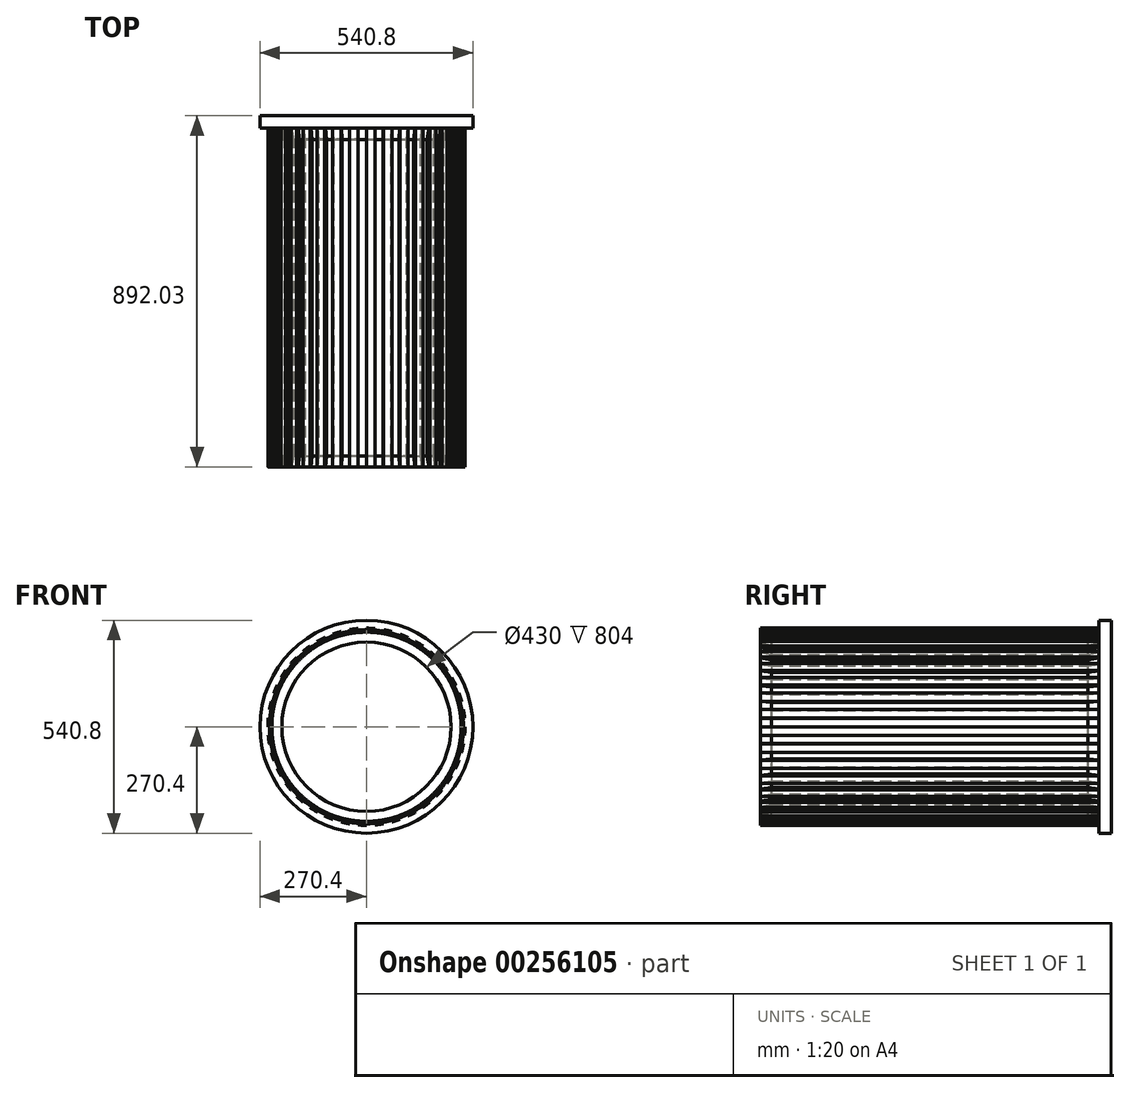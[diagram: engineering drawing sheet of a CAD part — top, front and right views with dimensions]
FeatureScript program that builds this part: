
annotation { "Feature Type Name" : "Feature", "Feature Type Description" : "" }
export const myFeature = defineFeature(function(context is Context, id is Id, definition is map)
    precondition{}
    {
        {
            var Q0;
            Q0=qCreatedBy(makeId("Front.planeOp"),FACE);
            var sketch = newSketch(context, id + "F0", { "sketchPlane" : qUnion([Q0])});
            skArc(sketch, "E0", {"start": v(-249.45, 21.82) * mm, "mid": v(-250.16, 10.92) * mm, "end": v(-250.4, 0) * mm});
            skArc(sketch, "E1", {"start": v(-236.75, 41.75) * mm, "mid": v(-238.34, 31.38) * mm, "end": v(-239.49, 20.95) * mm});
            skLineSegment(sketch, "E2", {"start": v(-239.49, 20.95) * mm, "end": v(-249.45, 21.82) * mm});
            skLineSegment(sketch, "E3", {"start": v(-236.75, 41.75) * mm, "end": v(-246.6, 43.48) * mm});
            skLineSegment(sketch, "E4.anchor1", {"start": v(0, 0) * mm, "end": v(-250.4, 0) * mm, "construction": true});
            skLineSegment(sketch, "E4.anchor2", {"start": v(0, 0) * mm, "end": v(-250.4, 0) * mm, "construction": true});
            skLineSegment(sketch, "E5.1.0", {"start": v(-225.9, 82.22) * mm, "end": v(-235.3, 85.64) * mm});
            skArc(sketch, "E5.1.1", {"start": v(-241.87, 64.8) * mm, "mid": v(-244.46, 54.2) * mm, "end": v(-246.6, 43.48) * mm});
            skLineSegment(sketch, "E5.1.2", {"start": v(-232.2, 62.22) * mm, "end": v(-241.87, 64.8) * mm});
            skArc(sketch, "E5.1.3", {"start": v(-225.9, 82.22) * mm, "mid": v(-229.27, 72.29) * mm, "end": v(-232.2, 62.22) * mm});
            skLineSegment(sketch, "E5.1.4", {"start": v(-225.9, 82.22) * mm, "end": v(-235.3, 85.64) * mm});
            skArc(sketch, "E5.1.5", {"start": v(-241.87, 64.8) * mm, "mid": v(-244.46, 54.2) * mm, "end": v(-246.6, 43.48) * mm});
            skLineSegment(sketch, "E5.1.6", {"start": v(-232.2, 62.22) * mm, "end": v(-241.87, 64.8) * mm});
            skArc(sketch, "E5.1.7", {"start": v(-225.9, 82.22) * mm, "mid": v(-229.27, 72.29) * mm, "end": v(-232.2, 62.22) * mm});
            skLineSegment(sketch, "E5.1.8", {"start": v(-225.9, 82.22) * mm, "end": v(-235.3, 85.64) * mm});
            skLineSegment(sketch, "E5.1.9", {"start": v(-232.2, 62.22) * mm, "end": v(-241.87, 64.8) * mm});
            skArc(sketch, "E5.1.10", {"start": v(-225.9, 82.22) * mm, "mid": v(-229.27, 72.29) * mm, "end": v(-232.2, 62.22) * mm});
            skArc(sketch, "E5.1.11", {"start": v(-241.87, 64.8) * mm, "mid": v(-244.46, 54.2) * mm, "end": v(-246.6, 43.48) * mm});
            skLineSegment(sketch, "E5.2.0", {"start": v(-208.2, 120.2) * mm, "end": v(-216.85, 125.2) * mm});
            skArc(sketch, "E5.2.1", {"start": v(-226.94, 105.82) * mm, "mid": v(-231.34, 95.82) * mm, "end": v(-235.3, 85.64) * mm});
            skLineSegment(sketch, "E5.2.2", {"start": v(-217.88, 101.6) * mm, "end": v(-226.94, 105.82) * mm});
            skArc(sketch, "E5.2.3", {"start": v(-208.2, 120.2) * mm, "mid": v(-213.24, 111) * mm, "end": v(-217.88, 101.6) * mm});
            skLineSegment(sketch, "E5.2.4", {"start": v(-208.2, 120.2) * mm, "end": v(-216.85, 125.2) * mm});
            skArc(sketch, "E5.2.5", {"start": v(-226.94, 105.82) * mm, "mid": v(-231.34, 95.82) * mm, "end": v(-235.3, 85.64) * mm});
            skLineSegment(sketch, "E5.2.6", {"start": v(-217.88, 101.6) * mm, "end": v(-226.94, 105.82) * mm});
            skArc(sketch, "E5.2.7", {"start": v(-208.2, 120.2) * mm, "mid": v(-213.24, 111) * mm, "end": v(-217.88, 101.6) * mm});
            skLineSegment(sketch, "E5.2.8", {"start": v(-208.2, 120.2) * mm, "end": v(-216.85, 125.2) * mm});
            skLineSegment(sketch, "E5.2.9", {"start": v(-217.88, 101.6) * mm, "end": v(-226.94, 105.82) * mm});
            skArc(sketch, "E5.2.10", {"start": v(-208.2, 120.2) * mm, "mid": v(-213.24, 111) * mm, "end": v(-217.88, 101.6) * mm});
            skArc(sketch, "E5.2.11", {"start": v(-226.94, 105.82) * mm, "mid": v(-231.34, 95.82) * mm, "end": v(-235.3, 85.64) * mm});
            skLineSegment(sketch, "E5.3.0", {"start": v(-184.16, 154.53) * mm, "end": v(-191.82, 160.95) * mm});
            skArc(sketch, "E5.3.1", {"start": v(-205.12, 143.62) * mm, "mid": v(-211.19, 134.54) * mm, "end": v(-216.85, 125.2) * mm});
            skLineSegment(sketch, "E5.3.2", {"start": v(-196.92, 137.89) * mm, "end": v(-205.12, 143.62) * mm});
            skArc(sketch, "E5.3.3", {"start": v(-184.16, 154.53) * mm, "mid": v(-190.72, 146.35) * mm, "end": v(-196.92, 137.89) * mm});
            skLineSegment(sketch, "E5.3.4", {"start": v(-184.16, 154.53) * mm, "end": v(-191.82, 160.95) * mm});
            skArc(sketch, "E5.3.5", {"start": v(-205.12, 143.62) * mm, "mid": v(-211.19, 134.54) * mm, "end": v(-216.85, 125.2) * mm});
            skLineSegment(sketch, "E5.3.6", {"start": v(-196.92, 137.89) * mm, "end": v(-205.12, 143.62) * mm});
            skArc(sketch, "E5.3.7", {"start": v(-184.16, 154.53) * mm, "mid": v(-190.72, 146.35) * mm, "end": v(-196.92, 137.89) * mm});
            skLineSegment(sketch, "E5.3.8", {"start": v(-184.16, 154.53) * mm, "end": v(-191.82, 160.95) * mm});
            skLineSegment(sketch, "E5.3.9", {"start": v(-196.92, 137.89) * mm, "end": v(-205.12, 143.62) * mm});
            skArc(sketch, "E5.3.10", {"start": v(-184.16, 154.53) * mm, "mid": v(-190.72, 146.35) * mm, "end": v(-196.92, 137.89) * mm});
            skArc(sketch, "E5.3.11", {"start": v(-205.12, 143.62) * mm, "mid": v(-211.19, 134.54) * mm, "end": v(-216.85, 125.2) * mm});
            skLineSegment(sketch, "E5.4.0", {"start": v(-154.53, 184.16) * mm, "end": v(-160.95, 191.82) * mm});
            skArc(sketch, "E5.4.1", {"start": v(-177.06, 177.06) * mm, "mid": v(-184.61, 169.17) * mm, "end": v(-191.82, 160.95) * mm});
            skLineSegment(sketch, "E5.4.2", {"start": v(-169.99, 169.99) * mm, "end": v(-177.06, 177.06) * mm});
            skArc(sketch, "E5.4.3", {"start": v(-154.53, 184.16) * mm, "mid": v(-162.41, 177.24) * mm, "end": v(-169.99, 169.99) * mm});
            skLineSegment(sketch, "E5.4.4", {"start": v(-154.53, 184.16) * mm, "end": v(-160.95, 191.82) * mm});
            skArc(sketch, "E5.4.5", {"start": v(-177.06, 177.06) * mm, "mid": v(-184.61, 169.17) * mm, "end": v(-191.82, 160.95) * mm});
            skLineSegment(sketch, "E5.4.6", {"start": v(-169.99, 169.99) * mm, "end": v(-177.06, 177.06) * mm});
            skArc(sketch, "E5.4.7", {"start": v(-154.53, 184.16) * mm, "mid": v(-162.41, 177.24) * mm, "end": v(-169.99, 169.99) * mm});
            skLineSegment(sketch, "E5.4.8", {"start": v(-154.53, 184.16) * mm, "end": v(-160.95, 191.82) * mm});
            skLineSegment(sketch, "E5.4.9", {"start": v(-169.99, 169.99) * mm, "end": v(-177.06, 177.06) * mm});
            skArc(sketch, "E5.4.10", {"start": v(-154.53, 184.16) * mm, "mid": v(-162.41, 177.24) * mm, "end": v(-169.99, 169.99) * mm});
            skArc(sketch, "E5.4.11", {"start": v(-177.06, 177.06) * mm, "mid": v(-184.61, 169.17) * mm, "end": v(-191.82, 160.95) * mm});
            skLineSegment(sketch, "E5.5.0", {"start": v(-120.2, 208.2) * mm, "end": v(-125.2, 216.85) * mm});
            skArc(sketch, "E5.5.1", {"start": v(-143.62, 205.12) * mm, "mid": v(-152.43, 198.66) * mm, "end": v(-160.95, 191.82) * mm});
            skLineSegment(sketch, "E5.5.2", {"start": v(-137.89, 196.92) * mm, "end": v(-143.62, 205.12) * mm});
            skArc(sketch, "E5.5.3", {"start": v(-120.2, 208.2) * mm, "mid": v(-129.17, 202.75) * mm, "end": v(-137.89, 196.92) * mm});
            skLineSegment(sketch, "E5.5.4", {"start": v(-120.2, 208.2) * mm, "end": v(-125.2, 216.85) * mm});
            skArc(sketch, "E5.5.5", {"start": v(-143.62, 205.12) * mm, "mid": v(-152.43, 198.66) * mm, "end": v(-160.95, 191.82) * mm});
            skLineSegment(sketch, "E5.5.6", {"start": v(-137.89, 196.92) * mm, "end": v(-143.62, 205.12) * mm});
            skArc(sketch, "E5.5.7", {"start": v(-120.2, 208.2) * mm, "mid": v(-129.17, 202.75) * mm, "end": v(-137.89, 196.92) * mm});
            skLineSegment(sketch, "E5.5.8", {"start": v(-120.2, 208.2) * mm, "end": v(-125.2, 216.85) * mm});
            skLineSegment(sketch, "E5.5.9", {"start": v(-137.89, 196.92) * mm, "end": v(-143.62, 205.12) * mm});
            skArc(sketch, "E5.5.10", {"start": v(-120.2, 208.2) * mm, "mid": v(-129.17, 202.75) * mm, "end": v(-137.89, 196.92) * mm});
            skArc(sketch, "E5.5.11", {"start": v(-143.62, 205.12) * mm, "mid": v(-152.43, 198.66) * mm, "end": v(-160.95, 191.82) * mm});
            skLineSegment(sketch, "E5.6.0", {"start": v(-82.22, 225.9) * mm, "end": v(-85.64, 235.3) * mm});
            skArc(sketch, "E5.6.1", {"start": v(-105.82, 226.94) * mm, "mid": v(-115.62, 222.1) * mm, "end": v(-125.2, 216.85) * mm});
            skLineSegment(sketch, "E5.6.2", {"start": v(-101.6, 217.88) * mm, "end": v(-105.82, 226.94) * mm});
            skArc(sketch, "E5.6.3", {"start": v(-82.22, 225.9) * mm, "mid": v(-92, 222.1) * mm, "end": v(-101.6, 217.88) * mm});
            skLineSegment(sketch, "E5.6.4", {"start": v(-82.22, 225.9) * mm, "end": v(-85.64, 235.3) * mm});
            skArc(sketch, "E5.6.5", {"start": v(-105.82, 226.94) * mm, "mid": v(-115.62, 222.1) * mm, "end": v(-125.2, 216.85) * mm});
            skLineSegment(sketch, "E5.6.6", {"start": v(-101.6, 217.88) * mm, "end": v(-105.82, 226.94) * mm});
            skArc(sketch, "E5.6.7", {"start": v(-82.22, 225.9) * mm, "mid": v(-92, 222.1) * mm, "end": v(-101.6, 217.88) * mm});
            skLineSegment(sketch, "E5.6.8", {"start": v(-82.22, 225.9) * mm, "end": v(-85.64, 235.3) * mm});
            skLineSegment(sketch, "E5.6.9", {"start": v(-101.6, 217.88) * mm, "end": v(-105.82, 226.94) * mm});
            skArc(sketch, "E5.6.10", {"start": v(-82.22, 225.9) * mm, "mid": v(-92, 222.1) * mm, "end": v(-101.6, 217.88) * mm});
            skArc(sketch, "E5.6.11", {"start": v(-105.82, 226.94) * mm, "mid": v(-115.62, 222.1) * mm, "end": v(-125.2, 216.85) * mm});
            skLineSegment(sketch, "E5.7.0", {"start": v(-41.75, 236.75) * mm, "end": v(-43.48, 246.6) * mm});
            skArc(sketch, "E5.7.1", {"start": v(-64.8, 241.87) * mm, "mid": v(-75.3, 238.81) * mm, "end": v(-85.64, 235.3) * mm});
            skLineSegment(sketch, "E5.7.2", {"start": v(-62.22, 232.2) * mm, "end": v(-64.8, 241.87) * mm});
            skArc(sketch, "E5.7.3", {"start": v(-41.75, 236.75) * mm, "mid": v(-52.03, 234.7) * mm, "end": v(-62.22, 232.2) * mm});
            skLineSegment(sketch, "E5.7.4", {"start": v(-41.75, 236.75) * mm, "end": v(-43.48, 246.6) * mm});
            skArc(sketch, "E5.7.5", {"start": v(-64.8, 241.87) * mm, "mid": v(-75.3, 238.81) * mm, "end": v(-85.64, 235.3) * mm});
            skLineSegment(sketch, "E5.7.6", {"start": v(-62.22, 232.2) * mm, "end": v(-64.8, 241.87) * mm});
            skArc(sketch, "E5.7.7", {"start": v(-41.75, 236.75) * mm, "mid": v(-52.03, 234.7) * mm, "end": v(-62.22, 232.2) * mm});
            skLineSegment(sketch, "E5.7.8", {"start": v(-41.75, 236.75) * mm, "end": v(-43.48, 246.6) * mm});
            skLineSegment(sketch, "E5.7.9", {"start": v(-62.22, 232.2) * mm, "end": v(-64.8, 241.87) * mm});
            skArc(sketch, "E5.7.10", {"start": v(-41.75, 236.75) * mm, "mid": v(-52.03, 234.7) * mm, "end": v(-62.22, 232.2) * mm});
            skArc(sketch, "E5.7.11", {"start": v(-64.8, 241.87) * mm, "mid": v(-75.3, 238.81) * mm, "end": v(-85.64, 235.3) * mm});
            skLineSegment(sketch, "E5.8.0", {"start": v(0, 240.4) * mm, "end": v(0, 250.4) * mm});
            skArc(sketch, "E5.8.1", {"start": v(-21.82, 249.45) * mm, "mid": v(-32.68, 248.26) * mm, "end": v(-43.48, 246.6) * mm});
            skLineSegment(sketch, "E5.8.2", {"start": v(-20.95, 239.49) * mm, "end": v(-21.82, 249.45) * mm});
            skArc(sketch, "E5.8.3", {"start": v(0, 240.4) * mm, "mid": v(-10.49, 240.17) * mm, "end": v(-20.95, 239.49) * mm});
            skLineSegment(sketch, "E5.8.4", {"start": v(0, 240.4) * mm, "end": v(0, 250.4) * mm});
            skArc(sketch, "E5.8.5", {"start": v(-21.82, 249.45) * mm, "mid": v(-32.68, 248.26) * mm, "end": v(-43.48, 246.6) * mm});
            skLineSegment(sketch, "E5.8.6", {"start": v(-20.95, 239.49) * mm, "end": v(-21.82, 249.45) * mm});
            skArc(sketch, "E5.8.7", {"start": v(0, 240.4) * mm, "mid": v(-10.49, 240.17) * mm, "end": v(-20.95, 239.49) * mm});
            skLineSegment(sketch, "E5.8.8", {"start": v(0, 240.4) * mm, "end": v(0, 250.4) * mm});
            skLineSegment(sketch, "E5.8.9", {"start": v(-20.95, 239.49) * mm, "end": v(-21.82, 249.45) * mm});
            skArc(sketch, "E5.8.10", {"start": v(0, 240.4) * mm, "mid": v(-10.49, 240.17) * mm, "end": v(-20.95, 239.49) * mm});
            skArc(sketch, "E5.8.11", {"start": v(-21.82, 249.45) * mm, "mid": v(-32.68, 248.26) * mm, "end": v(-43.48, 246.6) * mm});
            skLineSegment(sketch, "E5.9.0", {"start": v(41.75, 236.75) * mm, "end": v(43.48, 246.6) * mm});
            skArc(sketch, "E5.9.1", {"start": v(21.82, 249.45) * mm, "mid": v(10.92, 250.16) * mm, "end": v(0, 250.4) * mm});
            skLineSegment(sketch, "E5.9.2", {"start": v(20.95, 239.49) * mm, "end": v(21.82, 249.45) * mm});
            skArc(sketch, "E5.9.3", {"start": v(41.75, 236.75) * mm, "mid": v(31.38, 238.34) * mm, "end": v(20.95, 239.49) * mm});
            skLineSegment(sketch, "E5.9.4", {"start": v(41.75, 236.75) * mm, "end": v(43.48, 246.6) * mm});
            skArc(sketch, "E5.9.5", {"start": v(21.82, 249.45) * mm, "mid": v(10.92, 250.16) * mm, "end": v(0, 250.4) * mm});
            skLineSegment(sketch, "E5.9.6", {"start": v(20.95, 239.49) * mm, "end": v(21.82, 249.45) * mm});
            skArc(sketch, "E5.9.7", {"start": v(41.75, 236.75) * mm, "mid": v(31.38, 238.34) * mm, "end": v(20.95, 239.49) * mm});
            skLineSegment(sketch, "E5.9.8", {"start": v(41.75, 236.75) * mm, "end": v(43.48, 246.6) * mm});
            skLineSegment(sketch, "E5.9.9", {"start": v(20.95, 239.49) * mm, "end": v(21.82, 249.45) * mm});
            skArc(sketch, "E5.9.10", {"start": v(41.75, 236.75) * mm, "mid": v(31.38, 238.34) * mm, "end": v(20.95, 239.49) * mm});
            skArc(sketch, "E5.9.11", {"start": v(21.82, 249.45) * mm, "mid": v(10.92, 250.16) * mm, "end": v(0, 250.4) * mm});
            skLineSegment(sketch, "E5.10.0", {"start": v(82.22, 225.9) * mm, "end": v(85.64, 235.3) * mm});
            skArc(sketch, "E5.10.1", {"start": v(64.8, 241.87) * mm, "mid": v(54.2, 244.46) * mm, "end": v(43.48, 246.6) * mm});
            skLineSegment(sketch, "E5.10.2", {"start": v(62.22, 232.2) * mm, "end": v(64.8, 241.87) * mm});
            skArc(sketch, "E5.10.3", {"start": v(82.22, 225.9) * mm, "mid": v(72.29, 229.27) * mm, "end": v(62.22, 232.2) * mm});
            skLineSegment(sketch, "E5.10.4", {"start": v(82.22, 225.9) * mm, "end": v(85.64, 235.3) * mm});
            skArc(sketch, "E5.10.5", {"start": v(64.8, 241.87) * mm, "mid": v(54.2, 244.46) * mm, "end": v(43.48, 246.6) * mm});
            skLineSegment(sketch, "E5.10.6", {"start": v(62.22, 232.2) * mm, "end": v(64.8, 241.87) * mm});
            skArc(sketch, "E5.10.7", {"start": v(82.22, 225.9) * mm, "mid": v(72.29, 229.27) * mm, "end": v(62.22, 232.2) * mm});
            skLineSegment(sketch, "E5.10.8", {"start": v(82.22, 225.9) * mm, "end": v(85.64, 235.3) * mm});
            skLineSegment(sketch, "E5.10.9", {"start": v(62.22, 232.2) * mm, "end": v(64.8, 241.87) * mm});
            skArc(sketch, "E5.10.10", {"start": v(82.22, 225.9) * mm, "mid": v(72.29, 229.27) * mm, "end": v(62.22, 232.2) * mm});
            skArc(sketch, "E5.10.11", {"start": v(64.8, 241.87) * mm, "mid": v(54.2, 244.46) * mm, "end": v(43.48, 246.6) * mm});
            skLineSegment(sketch, "E5.11.0", {"start": v(120.2, 208.2) * mm, "end": v(125.2, 216.85) * mm});
            skArc(sketch, "E5.11.1", {"start": v(105.82, 226.94) * mm, "mid": v(95.82, 231.34) * mm, "end": v(85.64, 235.3) * mm});
            skLineSegment(sketch, "E5.11.2", {"start": v(101.6, 217.88) * mm, "end": v(105.82, 226.94) * mm});
            skArc(sketch, "E5.11.3", {"start": v(120.2, 208.2) * mm, "mid": v(111, 213.24) * mm, "end": v(101.6, 217.88) * mm});
            skLineSegment(sketch, "E5.11.4", {"start": v(120.2, 208.2) * mm, "end": v(125.2, 216.85) * mm});
            skArc(sketch, "E5.11.5", {"start": v(105.82, 226.94) * mm, "mid": v(95.82, 231.34) * mm, "end": v(85.64, 235.3) * mm});
            skLineSegment(sketch, "E5.11.6", {"start": v(101.6, 217.88) * mm, "end": v(105.82, 226.94) * mm});
            skArc(sketch, "E5.11.7", {"start": v(120.2, 208.2) * mm, "mid": v(111, 213.24) * mm, "end": v(101.6, 217.88) * mm});
            skLineSegment(sketch, "E5.11.8", {"start": v(120.2, 208.2) * mm, "end": v(125.2, 216.85) * mm});
            skLineSegment(sketch, "E5.11.9", {"start": v(101.6, 217.88) * mm, "end": v(105.82, 226.94) * mm});
            skArc(sketch, "E5.11.10", {"start": v(120.2, 208.2) * mm, "mid": v(111, 213.24) * mm, "end": v(101.6, 217.88) * mm});
            skArc(sketch, "E5.11.11", {"start": v(105.82, 226.94) * mm, "mid": v(95.82, 231.34) * mm, "end": v(85.64, 235.3) * mm});
            skLineSegment(sketch, "E5.12.0", {"start": v(154.53, 184.16) * mm, "end": v(160.95, 191.82) * mm});
            skArc(sketch, "E5.12.1", {"start": v(143.62, 205.12) * mm, "mid": v(134.54, 211.19) * mm, "end": v(125.2, 216.85) * mm});
            skLineSegment(sketch, "E5.12.2", {"start": v(137.89, 196.92) * mm, "end": v(143.62, 205.12) * mm});
            skArc(sketch, "E5.12.3", {"start": v(154.53, 184.16) * mm, "mid": v(146.35, 190.72) * mm, "end": v(137.89, 196.92) * mm});
            skLineSegment(sketch, "E5.12.4", {"start": v(154.53, 184.16) * mm, "end": v(160.95, 191.82) * mm});
            skArc(sketch, "E5.12.5", {"start": v(143.62, 205.12) * mm, "mid": v(134.54, 211.19) * mm, "end": v(125.2, 216.85) * mm});
            skLineSegment(sketch, "E5.12.6", {"start": v(137.89, 196.92) * mm, "end": v(143.62, 205.12) * mm});
            skArc(sketch, "E5.12.7", {"start": v(154.53, 184.16) * mm, "mid": v(146.35, 190.72) * mm, "end": v(137.89, 196.92) * mm});
            skLineSegment(sketch, "E5.12.8", {"start": v(154.53, 184.16) * mm, "end": v(160.95, 191.82) * mm});
            skLineSegment(sketch, "E5.12.9", {"start": v(137.89, 196.92) * mm, "end": v(143.62, 205.12) * mm});
            skArc(sketch, "E5.12.10", {"start": v(154.53, 184.16) * mm, "mid": v(146.35, 190.72) * mm, "end": v(137.89, 196.92) * mm});
            skArc(sketch, "E5.12.11", {"start": v(143.62, 205.12) * mm, "mid": v(134.54, 211.19) * mm, "end": v(125.2, 216.85) * mm});
            skLineSegment(sketch, "E5.13.0", {"start": v(184.16, 154.53) * mm, "end": v(191.82, 160.95) * mm});
            skArc(sketch, "E5.13.1", {"start": v(177.06, 177.06) * mm, "mid": v(169.17, 184.61) * mm, "end": v(160.95, 191.82) * mm});
            skLineSegment(sketch, "E5.13.2", {"start": v(169.99, 169.99) * mm, "end": v(177.06, 177.06) * mm});
            skArc(sketch, "E5.13.3", {"start": v(184.16, 154.53) * mm, "mid": v(177.24, 162.41) * mm, "end": v(169.99, 169.99) * mm});
            skLineSegment(sketch, "E5.13.4", {"start": v(184.16, 154.53) * mm, "end": v(191.82, 160.95) * mm});
            skArc(sketch, "E5.13.5", {"start": v(177.06, 177.06) * mm, "mid": v(169.17, 184.61) * mm, "end": v(160.95, 191.82) * mm});
            skLineSegment(sketch, "E5.13.6", {"start": v(169.99, 169.99) * mm, "end": v(177.06, 177.06) * mm});
            skArc(sketch, "E5.13.7", {"start": v(184.16, 154.53) * mm, "mid": v(177.24, 162.41) * mm, "end": v(169.99, 169.99) * mm});
            skLineSegment(sketch, "E5.13.8", {"start": v(184.16, 154.53) * mm, "end": v(191.82, 160.95) * mm});
            skLineSegment(sketch, "E5.13.9", {"start": v(169.99, 169.99) * mm, "end": v(177.06, 177.06) * mm});
            skArc(sketch, "E5.13.10", {"start": v(184.16, 154.53) * mm, "mid": v(177.24, 162.41) * mm, "end": v(169.99, 169.99) * mm});
            skArc(sketch, "E5.13.11", {"start": v(177.06, 177.06) * mm, "mid": v(169.17, 184.61) * mm, "end": v(160.95, 191.82) * mm});
            skLineSegment(sketch, "E5.14.0", {"start": v(208.2, 120.2) * mm, "end": v(216.85, 125.2) * mm});
            skArc(sketch, "E5.14.1", {"start": v(205.12, 143.62) * mm, "mid": v(198.66, 152.43) * mm, "end": v(191.82, 160.95) * mm});
            skLineSegment(sketch, "E5.14.2", {"start": v(196.92, 137.89) * mm, "end": v(205.12, 143.62) * mm});
            skArc(sketch, "E5.14.3", {"start": v(208.2, 120.2) * mm, "mid": v(202.75, 129.17) * mm, "end": v(196.92, 137.89) * mm});
            skLineSegment(sketch, "E5.14.4", {"start": v(208.2, 120.2) * mm, "end": v(216.85, 125.2) * mm});
            skArc(sketch, "E5.14.5", {"start": v(205.12, 143.62) * mm, "mid": v(198.66, 152.43) * mm, "end": v(191.82, 160.95) * mm});
            skLineSegment(sketch, "E5.14.6", {"start": v(196.92, 137.89) * mm, "end": v(205.12, 143.62) * mm});
            skArc(sketch, "E5.14.7", {"start": v(208.2, 120.2) * mm, "mid": v(202.75, 129.17) * mm, "end": v(196.92, 137.89) * mm});
            skLineSegment(sketch, "E5.14.8", {"start": v(208.2, 120.2) * mm, "end": v(216.85, 125.2) * mm});
            skLineSegment(sketch, "E5.14.9", {"start": v(196.92, 137.89) * mm, "end": v(205.12, 143.62) * mm});
            skArc(sketch, "E5.14.10", {"start": v(208.2, 120.2) * mm, "mid": v(202.75, 129.17) * mm, "end": v(196.92, 137.89) * mm});
            skArc(sketch, "E5.14.11", {"start": v(205.12, 143.62) * mm, "mid": v(198.66, 152.43) * mm, "end": v(191.82, 160.95) * mm});
            skLineSegment(sketch, "E5.15.0", {"start": v(225.9, 82.22) * mm, "end": v(235.3, 85.64) * mm});
            skArc(sketch, "E5.15.1", {"start": v(226.94, 105.82) * mm, "mid": v(222.1, 115.62) * mm, "end": v(216.85, 125.2) * mm});
            skLineSegment(sketch, "E5.15.2", {"start": v(217.88, 101.6) * mm, "end": v(226.94, 105.82) * mm});
            skArc(sketch, "E5.15.3", {"start": v(225.9, 82.22) * mm, "mid": v(222.1, 92) * mm, "end": v(217.88, 101.6) * mm});
            skLineSegment(sketch, "E5.15.4", {"start": v(225.9, 82.22) * mm, "end": v(235.3, 85.64) * mm});
            skArc(sketch, "E5.15.5", {"start": v(226.94, 105.82) * mm, "mid": v(222.1, 115.62) * mm, "end": v(216.85, 125.2) * mm});
            skLineSegment(sketch, "E5.15.6", {"start": v(217.88, 101.6) * mm, "end": v(226.94, 105.82) * mm});
            skArc(sketch, "E5.15.7", {"start": v(225.9, 82.22) * mm, "mid": v(222.1, 92) * mm, "end": v(217.88, 101.6) * mm});
            skLineSegment(sketch, "E5.15.8", {"start": v(225.9, 82.22) * mm, "end": v(235.3, 85.64) * mm});
            skLineSegment(sketch, "E5.15.9", {"start": v(217.88, 101.6) * mm, "end": v(226.94, 105.82) * mm});
            skArc(sketch, "E5.15.10", {"start": v(225.9, 82.22) * mm, "mid": v(222.1, 92) * mm, "end": v(217.88, 101.6) * mm});
            skArc(sketch, "E5.15.11", {"start": v(226.94, 105.82) * mm, "mid": v(222.1, 115.62) * mm, "end": v(216.85, 125.2) * mm});
            skLineSegment(sketch, "E5.16.0", {"start": v(236.75, 41.75) * mm, "end": v(246.6, 43.48) * mm});
            skArc(sketch, "E5.16.1", {"start": v(241.87, 64.8) * mm, "mid": v(238.81, 75.3) * mm, "end": v(235.3, 85.64) * mm});
            skLineSegment(sketch, "E5.16.2", {"start": v(232.2, 62.22) * mm, "end": v(241.87, 64.8) * mm});
            skArc(sketch, "E5.16.3", {"start": v(236.75, 41.75) * mm, "mid": v(234.7, 52.03) * mm, "end": v(232.2, 62.22) * mm});
            skLineSegment(sketch, "E5.16.4", {"start": v(236.75, 41.75) * mm, "end": v(246.6, 43.48) * mm});
            skArc(sketch, "E5.16.5", {"start": v(241.87, 64.8) * mm, "mid": v(238.81, 75.3) * mm, "end": v(235.3, 85.64) * mm});
            skLineSegment(sketch, "E5.16.6", {"start": v(232.2, 62.22) * mm, "end": v(241.87, 64.8) * mm});
            skArc(sketch, "E5.16.7", {"start": v(236.75, 41.75) * mm, "mid": v(234.7, 52.03) * mm, "end": v(232.2, 62.22) * mm});
            skLineSegment(sketch, "E5.16.8", {"start": v(236.75, 41.75) * mm, "end": v(246.6, 43.48) * mm});
            skLineSegment(sketch, "E5.16.9", {"start": v(232.2, 62.22) * mm, "end": v(241.87, 64.8) * mm});
            skArc(sketch, "E5.16.10", {"start": v(236.75, 41.75) * mm, "mid": v(234.7, 52.03) * mm, "end": v(232.2, 62.22) * mm});
            skArc(sketch, "E5.16.11", {"start": v(241.87, 64.8) * mm, "mid": v(238.81, 75.3) * mm, "end": v(235.3, 85.64) * mm});
            skLineSegment(sketch, "E5.17.0", {"start": v(240.4, 0) * mm, "end": v(250.4, 0) * mm});
            skArc(sketch, "E5.17.1", {"start": v(249.45, 21.82) * mm, "mid": v(248.26, 32.68) * mm, "end": v(246.6, 43.48) * mm});
            skLineSegment(sketch, "E5.17.2", {"start": v(239.49, 20.95) * mm, "end": v(249.45, 21.82) * mm});
            skArc(sketch, "E5.17.3", {"start": v(240.4, 0) * mm, "mid": v(240.17, 10.49) * mm, "end": v(239.49, 20.95) * mm});
            skLineSegment(sketch, "E5.17.4", {"start": v(240.4, 0) * mm, "end": v(250.4, 0) * mm});
            skArc(sketch, "E5.17.5", {"start": v(249.45, 21.82) * mm, "mid": v(248.26, 32.68) * mm, "end": v(246.6, 43.48) * mm});
            skLineSegment(sketch, "E5.17.6", {"start": v(239.49, 20.95) * mm, "end": v(249.45, 21.82) * mm});
            skArc(sketch, "E5.17.7", {"start": v(240.4, 0) * mm, "mid": v(240.17, 10.49) * mm, "end": v(239.49, 20.95) * mm});
            skLineSegment(sketch, "E5.17.8", {"start": v(240.4, 0) * mm, "end": v(250.4, 0) * mm});
            skLineSegment(sketch, "E5.17.9", {"start": v(239.49, 20.95) * mm, "end": v(249.45, 21.82) * mm});
            skArc(sketch, "E5.17.10", {"start": v(240.4, 0) * mm, "mid": v(240.17, 10.49) * mm, "end": v(239.49, 20.95) * mm});
            skArc(sketch, "E5.17.11", {"start": v(249.45, 21.82) * mm, "mid": v(248.26, 32.68) * mm, "end": v(246.6, 43.48) * mm});
            skLineSegment(sketch, "E5.18.0", {"start": v(236.75, -41.75) * mm, "end": v(246.6, -43.48) * mm});
            skArc(sketch, "E5.18.1", {"start": v(249.45, -21.82) * mm, "mid": v(250.16, -10.92) * mm, "end": v(250.4, 0) * mm});
            skLineSegment(sketch, "E5.18.2", {"start": v(239.49, -20.95) * mm, "end": v(249.45, -21.82) * mm});
            skArc(sketch, "E5.18.3", {"start": v(236.75, -41.75) * mm, "mid": v(238.34, -31.38) * mm, "end": v(239.49, -20.95) * mm});
            skLineSegment(sketch, "E5.18.4", {"start": v(236.75, -41.75) * mm, "end": v(246.6, -43.48) * mm});
            skArc(sketch, "E5.18.5", {"start": v(249.45, -21.82) * mm, "mid": v(250.16, -10.92) * mm, "end": v(250.4, 0) * mm});
            skLineSegment(sketch, "E5.18.6", {"start": v(239.49, -20.95) * mm, "end": v(249.45, -21.82) * mm});
            skArc(sketch, "E5.18.7", {"start": v(236.75, -41.75) * mm, "mid": v(238.34, -31.38) * mm, "end": v(239.49, -20.95) * mm});
            skLineSegment(sketch, "E5.18.8", {"start": v(236.75, -41.75) * mm, "end": v(246.6, -43.48) * mm});
            skLineSegment(sketch, "E5.18.9", {"start": v(239.49, -20.95) * mm, "end": v(249.45, -21.82) * mm});
            skArc(sketch, "E5.18.10", {"start": v(236.75, -41.75) * mm, "mid": v(238.34, -31.38) * mm, "end": v(239.49, -20.95) * mm});
            skArc(sketch, "E5.18.11", {"start": v(249.45, -21.82) * mm, "mid": v(250.16, -10.92) * mm, "end": v(250.4, 0) * mm});
            skLineSegment(sketch, "E5.19.0", {"start": v(225.9, -82.22) * mm, "end": v(235.3, -85.64) * mm});
            skArc(sketch, "E5.19.1", {"start": v(241.87, -64.8) * mm, "mid": v(244.46, -54.2) * mm, "end": v(246.6, -43.48) * mm});
            skLineSegment(sketch, "E5.19.2", {"start": v(232.2, -62.22) * mm, "end": v(241.87, -64.8) * mm});
            skArc(sketch, "E5.19.3", {"start": v(225.9, -82.22) * mm, "mid": v(229.27, -72.29) * mm, "end": v(232.2, -62.22) * mm});
            skLineSegment(sketch, "E5.19.4", {"start": v(225.9, -82.22) * mm, "end": v(235.3, -85.64) * mm});
            skArc(sketch, "E5.19.5", {"start": v(241.87, -64.8) * mm, "mid": v(244.46, -54.2) * mm, "end": v(246.6, -43.48) * mm});
            skLineSegment(sketch, "E5.19.6", {"start": v(232.2, -62.22) * mm, "end": v(241.87, -64.8) * mm});
            skArc(sketch, "E5.19.7", {"start": v(225.9, -82.22) * mm, "mid": v(229.27, -72.29) * mm, "end": v(232.2, -62.22) * mm});
            skLineSegment(sketch, "E5.19.8", {"start": v(225.9, -82.22) * mm, "end": v(235.3, -85.64) * mm});
            skLineSegment(sketch, "E5.19.9", {"start": v(232.2, -62.22) * mm, "end": v(241.87, -64.8) * mm});
            skArc(sketch, "E5.19.10", {"start": v(225.9, -82.22) * mm, "mid": v(229.27, -72.29) * mm, "end": v(232.2, -62.22) * mm});
            skArc(sketch, "E5.19.11", {"start": v(241.87, -64.8) * mm, "mid": v(244.46, -54.2) * mm, "end": v(246.6, -43.48) * mm});
            skLineSegment(sketch, "E5.20.0", {"start": v(208.2, -120.2) * mm, "end": v(216.85, -125.2) * mm});
            skArc(sketch, "E5.20.1", {"start": v(226.94, -105.82) * mm, "mid": v(231.34, -95.82) * mm, "end": v(235.3, -85.64) * mm});
            skLineSegment(sketch, "E5.20.2", {"start": v(217.88, -101.6) * mm, "end": v(226.94, -105.82) * mm});
            skArc(sketch, "E5.20.3", {"start": v(208.2, -120.2) * mm, "mid": v(213.24, -111) * mm, "end": v(217.88, -101.6) * mm});
            skLineSegment(sketch, "E5.20.4", {"start": v(208.2, -120.2) * mm, "end": v(216.85, -125.2) * mm});
            skArc(sketch, "E5.20.5", {"start": v(226.94, -105.82) * mm, "mid": v(231.34, -95.82) * mm, "end": v(235.3, -85.64) * mm});
            skLineSegment(sketch, "E5.20.6", {"start": v(217.88, -101.6) * mm, "end": v(226.94, -105.82) * mm});
            skArc(sketch, "E5.20.7", {"start": v(208.2, -120.2) * mm, "mid": v(213.24, -111) * mm, "end": v(217.88, -101.6) * mm});
            skLineSegment(sketch, "E5.20.8", {"start": v(208.2, -120.2) * mm, "end": v(216.85, -125.2) * mm});
            skLineSegment(sketch, "E5.20.9", {"start": v(217.88, -101.6) * mm, "end": v(226.94, -105.82) * mm});
            skArc(sketch, "E5.20.10", {"start": v(208.2, -120.2) * mm, "mid": v(213.24, -111) * mm, "end": v(217.88, -101.6) * mm});
            skArc(sketch, "E5.20.11", {"start": v(226.94, -105.82) * mm, "mid": v(231.34, -95.82) * mm, "end": v(235.3, -85.64) * mm});
            skLineSegment(sketch, "E5.21.0", {"start": v(184.16, -154.53) * mm, "end": v(191.82, -160.95) * mm});
            skArc(sketch, "E5.21.1", {"start": v(205.12, -143.62) * mm, "mid": v(211.19, -134.54) * mm, "end": v(216.85, -125.2) * mm});
            skLineSegment(sketch, "E5.21.2", {"start": v(196.92, -137.89) * mm, "end": v(205.12, -143.62) * mm});
            skArc(sketch, "E5.21.3", {"start": v(184.16, -154.53) * mm, "mid": v(190.72, -146.35) * mm, "end": v(196.92, -137.89) * mm});
            skLineSegment(sketch, "E5.21.4", {"start": v(184.16, -154.53) * mm, "end": v(191.82, -160.95) * mm});
            skArc(sketch, "E5.21.5", {"start": v(205.12, -143.62) * mm, "mid": v(211.19, -134.54) * mm, "end": v(216.85, -125.2) * mm});
            skLineSegment(sketch, "E5.21.6", {"start": v(196.92, -137.89) * mm, "end": v(205.12, -143.62) * mm});
            skArc(sketch, "E5.21.7", {"start": v(184.16, -154.53) * mm, "mid": v(190.72, -146.35) * mm, "end": v(196.92, -137.89) * mm});
            skLineSegment(sketch, "E5.21.8", {"start": v(184.16, -154.53) * mm, "end": v(191.82, -160.95) * mm});
            skLineSegment(sketch, "E5.21.9", {"start": v(196.92, -137.89) * mm, "end": v(205.12, -143.62) * mm});
            skArc(sketch, "E5.21.10", {"start": v(184.16, -154.53) * mm, "mid": v(190.72, -146.35) * mm, "end": v(196.92, -137.89) * mm});
            skArc(sketch, "E5.21.11", {"start": v(205.12, -143.62) * mm, "mid": v(211.19, -134.54) * mm, "end": v(216.85, -125.2) * mm});
            skLineSegment(sketch, "E5.22.0", {"start": v(154.53, -184.16) * mm, "end": v(160.95, -191.82) * mm});
            skArc(sketch, "E5.22.1", {"start": v(177.06, -177.06) * mm, "mid": v(184.61, -169.17) * mm, "end": v(191.82, -160.95) * mm});
            skLineSegment(sketch, "E5.22.2", {"start": v(169.99, -169.99) * mm, "end": v(177.06, -177.06) * mm});
            skArc(sketch, "E5.22.3", {"start": v(154.53, -184.16) * mm, "mid": v(162.41, -177.24) * mm, "end": v(169.99, -169.99) * mm});
            skLineSegment(sketch, "E5.22.4", {"start": v(154.53, -184.16) * mm, "end": v(160.95, -191.82) * mm});
            skArc(sketch, "E5.22.5", {"start": v(177.06, -177.06) * mm, "mid": v(184.61, -169.17) * mm, "end": v(191.82, -160.95) * mm});
            skLineSegment(sketch, "E5.22.6", {"start": v(169.99, -169.99) * mm, "end": v(177.06, -177.06) * mm});
            skArc(sketch, "E5.22.7", {"start": v(154.53, -184.16) * mm, "mid": v(162.41, -177.24) * mm, "end": v(169.99, -169.99) * mm});
            skLineSegment(sketch, "E5.22.8", {"start": v(154.53, -184.16) * mm, "end": v(160.95, -191.82) * mm});
            skLineSegment(sketch, "E5.22.9", {"start": v(169.99, -169.99) * mm, "end": v(177.06, -177.06) * mm});
            skArc(sketch, "E5.22.10", {"start": v(154.53, -184.16) * mm, "mid": v(162.41, -177.24) * mm, "end": v(169.99, -169.99) * mm});
            skArc(sketch, "E5.22.11", {"start": v(177.06, -177.06) * mm, "mid": v(184.61, -169.17) * mm, "end": v(191.82, -160.95) * mm});
            skLineSegment(sketch, "E5.23.0", {"start": v(120.2, -208.2) * mm, "end": v(125.2, -216.85) * mm});
            skArc(sketch, "E5.23.1", {"start": v(143.62, -205.12) * mm, "mid": v(152.43, -198.66) * mm, "end": v(160.95, -191.82) * mm});
            skLineSegment(sketch, "E5.23.2", {"start": v(137.89, -196.92) * mm, "end": v(143.62, -205.12) * mm});
            skArc(sketch, "E5.23.3", {"start": v(120.2, -208.2) * mm, "mid": v(129.17, -202.75) * mm, "end": v(137.89, -196.92) * mm});
            skLineSegment(sketch, "E5.23.4", {"start": v(120.2, -208.2) * mm, "end": v(125.2, -216.85) * mm});
            skArc(sketch, "E5.23.5", {"start": v(143.62, -205.12) * mm, "mid": v(152.43, -198.66) * mm, "end": v(160.95, -191.82) * mm});
            skLineSegment(sketch, "E5.23.6", {"start": v(137.89, -196.92) * mm, "end": v(143.62, -205.12) * mm});
            skArc(sketch, "E5.23.7", {"start": v(120.2, -208.2) * mm, "mid": v(129.17, -202.75) * mm, "end": v(137.89, -196.92) * mm});
            skLineSegment(sketch, "E5.23.8", {"start": v(120.2, -208.2) * mm, "end": v(125.2, -216.85) * mm});
            skLineSegment(sketch, "E5.23.9", {"start": v(137.89, -196.92) * mm, "end": v(143.62, -205.12) * mm});
            skArc(sketch, "E5.23.10", {"start": v(120.2, -208.2) * mm, "mid": v(129.17, -202.75) * mm, "end": v(137.89, -196.92) * mm});
            skArc(sketch, "E5.23.11", {"start": v(143.62, -205.12) * mm, "mid": v(152.43, -198.66) * mm, "end": v(160.95, -191.82) * mm});
            skLineSegment(sketch, "E5.24.0", {"start": v(82.22, -225.9) * mm, "end": v(85.64, -235.3) * mm});
            skArc(sketch, "E5.24.1", {"start": v(105.82, -226.94) * mm, "mid": v(115.62, -222.1) * mm, "end": v(125.2, -216.85) * mm});
            skLineSegment(sketch, "E5.24.2", {"start": v(101.6, -217.88) * mm, "end": v(105.82, -226.94) * mm});
            skArc(sketch, "E5.24.3", {"start": v(82.22, -225.9) * mm, "mid": v(92, -222.1) * mm, "end": v(101.6, -217.88) * mm});
            skLineSegment(sketch, "E5.24.4", {"start": v(82.22, -225.9) * mm, "end": v(85.64, -235.3) * mm});
            skArc(sketch, "E5.24.5", {"start": v(105.82, -226.94) * mm, "mid": v(115.62, -222.1) * mm, "end": v(125.2, -216.85) * mm});
            skLineSegment(sketch, "E5.24.6", {"start": v(101.6, -217.88) * mm, "end": v(105.82, -226.94) * mm});
            skArc(sketch, "E5.24.7", {"start": v(82.22, -225.9) * mm, "mid": v(92, -222.1) * mm, "end": v(101.6, -217.88) * mm});
            skLineSegment(sketch, "E5.24.8", {"start": v(82.22, -225.9) * mm, "end": v(85.64, -235.3) * mm});
            skLineSegment(sketch, "E5.24.9", {"start": v(101.6, -217.88) * mm, "end": v(105.82, -226.94) * mm});
            skArc(sketch, "E5.24.10", {"start": v(82.22, -225.9) * mm, "mid": v(92, -222.1) * mm, "end": v(101.6, -217.88) * mm});
            skArc(sketch, "E5.24.11", {"start": v(105.82, -226.94) * mm, "mid": v(115.62, -222.1) * mm, "end": v(125.2, -216.85) * mm});
            skLineSegment(sketch, "E5.25.0", {"start": v(41.75, -236.75) * mm, "end": v(43.48, -246.6) * mm});
            skArc(sketch, "E5.25.1", {"start": v(64.8, -241.87) * mm, "mid": v(75.3, -238.81) * mm, "end": v(85.64, -235.3) * mm});
            skLineSegment(sketch, "E5.25.2", {"start": v(62.22, -232.2) * mm, "end": v(64.8, -241.87) * mm});
            skArc(sketch, "E5.25.3", {"start": v(41.75, -236.75) * mm, "mid": v(52.03, -234.7) * mm, "end": v(62.22, -232.2) * mm});
            skLineSegment(sketch, "E5.25.4", {"start": v(41.75, -236.75) * mm, "end": v(43.48, -246.6) * mm});
            skArc(sketch, "E5.25.5", {"start": v(64.8, -241.87) * mm, "mid": v(75.3, -238.81) * mm, "end": v(85.64, -235.3) * mm});
            skLineSegment(sketch, "E5.25.6", {"start": v(62.22, -232.2) * mm, "end": v(64.8, -241.87) * mm});
            skArc(sketch, "E5.25.7", {"start": v(41.75, -236.75) * mm, "mid": v(52.03, -234.7) * mm, "end": v(62.22, -232.2) * mm});
            skLineSegment(sketch, "E5.25.8", {"start": v(41.75, -236.75) * mm, "end": v(43.48, -246.6) * mm});
            skLineSegment(sketch, "E5.25.9", {"start": v(62.22, -232.2) * mm, "end": v(64.8, -241.87) * mm});
            skArc(sketch, "E5.25.10", {"start": v(41.75, -236.75) * mm, "mid": v(52.03, -234.7) * mm, "end": v(62.22, -232.2) * mm});
            skArc(sketch, "E5.25.11", {"start": v(64.8, -241.87) * mm, "mid": v(75.3, -238.81) * mm, "end": v(85.64, -235.3) * mm});
            skLineSegment(sketch, "E5.26.0", {"start": v(0, -240.4) * mm, "end": v(0, -250.4) * mm});
            skArc(sketch, "E5.26.1", {"start": v(21.82, -249.45) * mm, "mid": v(32.68, -248.26) * mm, "end": v(43.48, -246.6) * mm});
            skLineSegment(sketch, "E5.26.2", {"start": v(20.95, -239.49) * mm, "end": v(21.82, -249.45) * mm});
            skArc(sketch, "E5.26.3", {"start": v(0, -240.4) * mm, "mid": v(10.49, -240.17) * mm, "end": v(20.95, -239.49) * mm});
            skLineSegment(sketch, "E5.26.4", {"start": v(0, -240.4) * mm, "end": v(0, -250.4) * mm});
            skArc(sketch, "E5.26.5", {"start": v(21.82, -249.45) * mm, "mid": v(32.68, -248.26) * mm, "end": v(43.48, -246.6) * mm});
            skLineSegment(sketch, "E5.26.6", {"start": v(20.95, -239.49) * mm, "end": v(21.82, -249.45) * mm});
            skArc(sketch, "E5.26.7", {"start": v(0, -240.4) * mm, "mid": v(10.49, -240.17) * mm, "end": v(20.95, -239.49) * mm});
            skLineSegment(sketch, "E5.26.8", {"start": v(0, -240.4) * mm, "end": v(0, -250.4) * mm});
            skLineSegment(sketch, "E5.26.9", {"start": v(20.95, -239.49) * mm, "end": v(21.82, -249.45) * mm});
            skArc(sketch, "E5.26.10", {"start": v(0, -240.4) * mm, "mid": v(10.49, -240.17) * mm, "end": v(20.95, -239.49) * mm});
            skArc(sketch, "E5.26.11", {"start": v(21.82, -249.45) * mm, "mid": v(32.68, -248.26) * mm, "end": v(43.48, -246.6) * mm});
            skLineSegment(sketch, "E5.27.0", {"start": v(-41.75, -236.75) * mm, "end": v(-43.48, -246.6) * mm});
            skArc(sketch, "E5.27.1", {"start": v(-21.82, -249.45) * mm, "mid": v(-10.92, -250.16) * mm, "end": v(0, -250.4) * mm});
            skLineSegment(sketch, "E5.27.2", {"start": v(-20.95, -239.49) * mm, "end": v(-21.82, -249.45) * mm});
            skArc(sketch, "E5.27.3", {"start": v(-41.75, -236.75) * mm, "mid": v(-31.38, -238.34) * mm, "end": v(-20.95, -239.49) * mm});
            skLineSegment(sketch, "E5.27.4", {"start": v(-41.75, -236.75) * mm, "end": v(-43.48, -246.6) * mm});
            skArc(sketch, "E5.27.5", {"start": v(-21.82, -249.45) * mm, "mid": v(-10.92, -250.16) * mm, "end": v(0, -250.4) * mm});
            skLineSegment(sketch, "E5.27.6", {"start": v(-20.95, -239.49) * mm, "end": v(-21.82, -249.45) * mm});
            skArc(sketch, "E5.27.7", {"start": v(-41.75, -236.75) * mm, "mid": v(-31.38, -238.34) * mm, "end": v(-20.95, -239.49) * mm});
            skLineSegment(sketch, "E5.27.8", {"start": v(-41.75, -236.75) * mm, "end": v(-43.48, -246.6) * mm});
            skLineSegment(sketch, "E5.27.9", {"start": v(-20.95, -239.49) * mm, "end": v(-21.82, -249.45) * mm});
            skArc(sketch, "E5.27.10", {"start": v(-41.75, -236.75) * mm, "mid": v(-31.38, -238.34) * mm, "end": v(-20.95, -239.49) * mm});
            skArc(sketch, "E5.27.11", {"start": v(-21.82, -249.45) * mm, "mid": v(-10.92, -250.16) * mm, "end": v(0, -250.4) * mm});
            skLineSegment(sketch, "E5.28.0", {"start": v(-82.22, -225.9) * mm, "end": v(-85.64, -235.3) * mm});
            skArc(sketch, "E5.28.1", {"start": v(-64.8, -241.87) * mm, "mid": v(-54.2, -244.46) * mm, "end": v(-43.48, -246.6) * mm});
            skLineSegment(sketch, "E5.28.2", {"start": v(-62.22, -232.2) * mm, "end": v(-64.8, -241.87) * mm});
            skArc(sketch, "E5.28.3", {"start": v(-82.22, -225.9) * mm, "mid": v(-72.29, -229.27) * mm, "end": v(-62.22, -232.2) * mm});
            skLineSegment(sketch, "E5.28.4", {"start": v(-82.22, -225.9) * mm, "end": v(-85.64, -235.3) * mm});
            skArc(sketch, "E5.28.5", {"start": v(-64.8, -241.87) * mm, "mid": v(-54.2, -244.46) * mm, "end": v(-43.48, -246.6) * mm});
            skLineSegment(sketch, "E5.28.6", {"start": v(-62.22, -232.2) * mm, "end": v(-64.8, -241.87) * mm});
            skArc(sketch, "E5.28.7", {"start": v(-82.22, -225.9) * mm, "mid": v(-72.29, -229.27) * mm, "end": v(-62.22, -232.2) * mm});
            skLineSegment(sketch, "E5.28.8", {"start": v(-82.22, -225.9) * mm, "end": v(-85.64, -235.3) * mm});
            skLineSegment(sketch, "E5.28.9", {"start": v(-62.22, -232.2) * mm, "end": v(-64.8, -241.87) * mm});
            skArc(sketch, "E5.28.10", {"start": v(-82.22, -225.9) * mm, "mid": v(-72.29, -229.27) * mm, "end": v(-62.22, -232.2) * mm});
            skArc(sketch, "E5.28.11", {"start": v(-64.8, -241.87) * mm, "mid": v(-54.2, -244.46) * mm, "end": v(-43.48, -246.6) * mm});
            skLineSegment(sketch, "E5.29.0", {"start": v(-120.2, -208.2) * mm, "end": v(-125.2, -216.85) * mm});
            skArc(sketch, "E5.29.1", {"start": v(-105.82, -226.94) * mm, "mid": v(-95.82, -231.34) * mm, "end": v(-85.64, -235.3) * mm});
            skLineSegment(sketch, "E5.29.2", {"start": v(-101.6, -217.88) * mm, "end": v(-105.82, -226.94) * mm});
            skArc(sketch, "E5.29.3", {"start": v(-120.2, -208.2) * mm, "mid": v(-111, -213.24) * mm, "end": v(-101.6, -217.88) * mm});
            skLineSegment(sketch, "E5.29.4", {"start": v(-120.2, -208.2) * mm, "end": v(-125.2, -216.85) * mm});
            skArc(sketch, "E5.29.5", {"start": v(-105.82, -226.94) * mm, "mid": v(-95.82, -231.34) * mm, "end": v(-85.64, -235.3) * mm});
            skLineSegment(sketch, "E5.29.6", {"start": v(-101.6, -217.88) * mm, "end": v(-105.82, -226.94) * mm});
            skArc(sketch, "E5.29.7", {"start": v(-120.2, -208.2) * mm, "mid": v(-111, -213.24) * mm, "end": v(-101.6, -217.88) * mm});
            skLineSegment(sketch, "E5.29.8", {"start": v(-120.2, -208.2) * mm, "end": v(-125.2, -216.85) * mm});
            skLineSegment(sketch, "E5.29.9", {"start": v(-101.6, -217.88) * mm, "end": v(-105.82, -226.94) * mm});
            skArc(sketch, "E5.29.10", {"start": v(-120.2, -208.2) * mm, "mid": v(-111, -213.24) * mm, "end": v(-101.6, -217.88) * mm});
            skArc(sketch, "E5.29.11", {"start": v(-105.82, -226.94) * mm, "mid": v(-95.82, -231.34) * mm, "end": v(-85.64, -235.3) * mm});
            skLineSegment(sketch, "E5.30.0", {"start": v(-154.53, -184.16) * mm, "end": v(-160.95, -191.82) * mm});
            skArc(sketch, "E5.30.1", {"start": v(-143.62, -205.12) * mm, "mid": v(-134.54, -211.19) * mm, "end": v(-125.2, -216.85) * mm});
            skLineSegment(sketch, "E5.30.2", {"start": v(-137.89, -196.92) * mm, "end": v(-143.62, -205.12) * mm});
            skArc(sketch, "E5.30.3", {"start": v(-154.53, -184.16) * mm, "mid": v(-146.35, -190.72) * mm, "end": v(-137.89, -196.92) * mm});
            skLineSegment(sketch, "E5.30.4", {"start": v(-154.53, -184.16) * mm, "end": v(-160.95, -191.82) * mm});
            skArc(sketch, "E5.30.5", {"start": v(-143.62, -205.12) * mm, "mid": v(-134.54, -211.19) * mm, "end": v(-125.2, -216.85) * mm});
            skLineSegment(sketch, "E5.30.6", {"start": v(-137.89, -196.92) * mm, "end": v(-143.62, -205.12) * mm});
            skArc(sketch, "E5.30.7", {"start": v(-154.53, -184.16) * mm, "mid": v(-146.35, -190.72) * mm, "end": v(-137.89, -196.92) * mm});
            skLineSegment(sketch, "E5.30.8", {"start": v(-154.53, -184.16) * mm, "end": v(-160.95, -191.82) * mm});
            skLineSegment(sketch, "E5.30.9", {"start": v(-137.89, -196.92) * mm, "end": v(-143.62, -205.12) * mm});
            skArc(sketch, "E5.30.10", {"start": v(-154.53, -184.16) * mm, "mid": v(-146.35, -190.72) * mm, "end": v(-137.89, -196.92) * mm});
            skArc(sketch, "E5.30.11", {"start": v(-143.62, -205.12) * mm, "mid": v(-134.54, -211.19) * mm, "end": v(-125.2, -216.85) * mm});
            skLineSegment(sketch, "E5.31.0", {"start": v(-184.16, -154.53) * mm, "end": v(-191.82, -160.95) * mm});
            skArc(sketch, "E5.31.1", {"start": v(-177.06, -177.06) * mm, "mid": v(-169.17, -184.61) * mm, "end": v(-160.95, -191.82) * mm});
            skLineSegment(sketch, "E5.31.2", {"start": v(-169.99, -169.99) * mm, "end": v(-177.06, -177.06) * mm});
            skArc(sketch, "E5.31.3", {"start": v(-184.16, -154.53) * mm, "mid": v(-177.24, -162.41) * mm, "end": v(-169.99, -169.99) * mm});
            skLineSegment(sketch, "E5.31.4", {"start": v(-184.16, -154.53) * mm, "end": v(-191.82, -160.95) * mm});
            skArc(sketch, "E5.31.5", {"start": v(-177.06, -177.06) * mm, "mid": v(-169.17, -184.61) * mm, "end": v(-160.95, -191.82) * mm});
            skLineSegment(sketch, "E5.31.6", {"start": v(-169.99, -169.99) * mm, "end": v(-177.06, -177.06) * mm});
            skArc(sketch, "E5.31.7", {"start": v(-184.16, -154.53) * mm, "mid": v(-177.24, -162.41) * mm, "end": v(-169.99, -169.99) * mm});
            skLineSegment(sketch, "E5.31.8", {"start": v(-184.16, -154.53) * mm, "end": v(-191.82, -160.95) * mm});
            skLineSegment(sketch, "E5.31.9", {"start": v(-169.99, -169.99) * mm, "end": v(-177.06, -177.06) * mm});
            skArc(sketch, "E5.31.10", {"start": v(-184.16, -154.53) * mm, "mid": v(-177.24, -162.41) * mm, "end": v(-169.99, -169.99) * mm});
            skArc(sketch, "E5.31.11", {"start": v(-177.06, -177.06) * mm, "mid": v(-169.17, -184.61) * mm, "end": v(-160.95, -191.82) * mm});
            skLineSegment(sketch, "E5.32.0", {"start": v(-208.2, -120.2) * mm, "end": v(-216.85, -125.2) * mm});
            skArc(sketch, "E5.32.1", {"start": v(-205.12, -143.62) * mm, "mid": v(-198.66, -152.43) * mm, "end": v(-191.82, -160.95) * mm});
            skLineSegment(sketch, "E5.32.2", {"start": v(-196.92, -137.89) * mm, "end": v(-205.12, -143.62) * mm});
            skArc(sketch, "E5.32.3", {"start": v(-208.2, -120.2) * mm, "mid": v(-202.75, -129.17) * mm, "end": v(-196.92, -137.89) * mm});
            skLineSegment(sketch, "E5.32.4", {"start": v(-208.2, -120.2) * mm, "end": v(-216.85, -125.2) * mm});
            skArc(sketch, "E5.32.5", {"start": v(-205.12, -143.62) * mm, "mid": v(-198.66, -152.43) * mm, "end": v(-191.82, -160.95) * mm});
            skLineSegment(sketch, "E5.32.6", {"start": v(-196.92, -137.89) * mm, "end": v(-205.12, -143.62) * mm});
            skArc(sketch, "E5.32.7", {"start": v(-208.2, -120.2) * mm, "mid": v(-202.75, -129.17) * mm, "end": v(-196.92, -137.89) * mm});
            skLineSegment(sketch, "E5.32.8", {"start": v(-208.2, -120.2) * mm, "end": v(-216.85, -125.2) * mm});
            skLineSegment(sketch, "E5.32.9", {"start": v(-196.92, -137.89) * mm, "end": v(-205.12, -143.62) * mm});
            skArc(sketch, "E5.32.10", {"start": v(-208.2, -120.2) * mm, "mid": v(-202.75, -129.17) * mm, "end": v(-196.92, -137.89) * mm});
            skArc(sketch, "E5.32.11", {"start": v(-205.12, -143.62) * mm, "mid": v(-198.66, -152.43) * mm, "end": v(-191.82, -160.95) * mm});
            skLineSegment(sketch, "E5.33.0", {"start": v(-225.9, -82.22) * mm, "end": v(-235.3, -85.64) * mm});
            skArc(sketch, "E5.33.1", {"start": v(-226.94, -105.82) * mm, "mid": v(-222.1, -115.62) * mm, "end": v(-216.85, -125.2) * mm});
            skLineSegment(sketch, "E5.33.2", {"start": v(-217.88, -101.6) * mm, "end": v(-226.94, -105.82) * mm});
            skArc(sketch, "E5.33.3", {"start": v(-225.9, -82.22) * mm, "mid": v(-222.1, -92) * mm, "end": v(-217.88, -101.6) * mm});
            skLineSegment(sketch, "E5.33.4", {"start": v(-225.9, -82.22) * mm, "end": v(-235.3, -85.64) * mm});
            skArc(sketch, "E5.33.5", {"start": v(-226.94, -105.82) * mm, "mid": v(-222.1, -115.62) * mm, "end": v(-216.85, -125.2) * mm});
            skLineSegment(sketch, "E5.33.6", {"start": v(-217.88, -101.6) * mm, "end": v(-226.94, -105.82) * mm});
            skArc(sketch, "E5.33.7", {"start": v(-225.9, -82.22) * mm, "mid": v(-222.1, -92) * mm, "end": v(-217.88, -101.6) * mm});
            skLineSegment(sketch, "E5.33.8", {"start": v(-225.9, -82.22) * mm, "end": v(-235.3, -85.64) * mm});
            skLineSegment(sketch, "E5.33.9", {"start": v(-217.88, -101.6) * mm, "end": v(-226.94, -105.82) * mm});
            skArc(sketch, "E5.33.10", {"start": v(-225.9, -82.22) * mm, "mid": v(-222.1, -92) * mm, "end": v(-217.88, -101.6) * mm});
            skArc(sketch, "E5.33.11", {"start": v(-226.94, -105.82) * mm, "mid": v(-222.1, -115.62) * mm, "end": v(-216.85, -125.2) * mm});
            skLineSegment(sketch, "E5.34.0", {"start": v(-236.75, -41.75) * mm, "end": v(-246.6, -43.48) * mm});
            skArc(sketch, "E5.34.1", {"start": v(-241.87, -64.8) * mm, "mid": v(-238.81, -75.3) * mm, "end": v(-235.3, -85.64) * mm});
            skLineSegment(sketch, "E5.34.2", {"start": v(-232.2, -62.22) * mm, "end": v(-241.87, -64.8) * mm});
            skArc(sketch, "E5.34.3", {"start": v(-236.75, -41.75) * mm, "mid": v(-234.7, -52.03) * mm, "end": v(-232.2, -62.22) * mm});
            skLineSegment(sketch, "E5.34.4", {"start": v(-236.75, -41.75) * mm, "end": v(-246.6, -43.48) * mm});
            skArc(sketch, "E5.34.5", {"start": v(-241.87, -64.8) * mm, "mid": v(-238.81, -75.3) * mm, "end": v(-235.3, -85.64) * mm});
            skLineSegment(sketch, "E5.34.6", {"start": v(-232.2, -62.22) * mm, "end": v(-241.87, -64.8) * mm});
            skArc(sketch, "E5.34.7", {"start": v(-236.75, -41.75) * mm, "mid": v(-234.7, -52.03) * mm, "end": v(-232.2, -62.22) * mm});
            skLineSegment(sketch, "E5.34.8", {"start": v(-236.75, -41.75) * mm, "end": v(-246.6, -43.48) * mm});
            skLineSegment(sketch, "E5.34.9", {"start": v(-232.2, -62.22) * mm, "end": v(-241.87, -64.8) * mm});
            skArc(sketch, "E5.34.10", {"start": v(-236.75, -41.75) * mm, "mid": v(-234.7, -52.03) * mm, "end": v(-232.2, -62.22) * mm});
            skArc(sketch, "E5.34.11", {"start": v(-241.87, -64.8) * mm, "mid": v(-238.81, -75.3) * mm, "end": v(-235.3, -85.64) * mm});
            skLineSegment(sketch, "E5.35.0", {"start": v(-240.4, 0) * mm, "end": v(-250.4, 0) * mm});
            skArc(sketch, "E5.35.1", {"start": v(-249.45, -21.82) * mm, "mid": v(-248.26, -32.68) * mm, "end": v(-246.6, -43.48) * mm});
            skLineSegment(sketch, "E5.35.2", {"start": v(-239.49, -20.95) * mm, "end": v(-249.45, -21.82) * mm});
            skArc(sketch, "E5.35.3", {"start": v(-240.4, 0) * mm, "mid": v(-240.17, -10.49) * mm, "end": v(-239.49, -20.95) * mm});
            skLineSegment(sketch, "E5.35.4", {"start": v(-240.4, 0) * mm, "end": v(-250.4, 0) * mm});
            skArc(sketch, "E5.35.5", {"start": v(-249.45, -21.82) * mm, "mid": v(-248.26, -32.68) * mm, "end": v(-246.6, -43.48) * mm});
            skLineSegment(sketch, "E5.35.6", {"start": v(-239.49, -20.95) * mm, "end": v(-249.45, -21.82) * mm});
            skArc(sketch, "E5.35.7", {"start": v(-240.4, 0) * mm, "mid": v(-240.17, -10.49) * mm, "end": v(-239.49, -20.95) * mm});
            skLineSegment(sketch, "E5.35.8", {"start": v(-240.4, 0) * mm, "end": v(-250.4, 0) * mm});
            skLineSegment(sketch, "E5.35.9", {"start": v(-239.49, -20.95) * mm, "end": v(-249.45, -21.82) * mm});
            skArc(sketch, "E5.35.10", {"start": v(-240.4, 0) * mm, "mid": v(-240.17, -10.49) * mm, "end": v(-239.49, -20.95) * mm});
            skArc(sketch, "E5.35.11", {"start": v(-249.45, -21.82) * mm, "mid": v(-248.26, -32.68) * mm, "end": v(-246.6, -43.48) * mm});
            skLineSegment(sketch, "E5.anchor2", {"start": v(0, 0) * mm, "end": v(-246.6, -43.48) * mm, "construction": true});
            skCircle(sketch, "E6", {"center": v(0, 0) * mm, "radius": 215 * mm});
            skSolve(sketch);
        }
        {
            var Q0;
            Q0 = qSketchRegion(id + "F0", true);
            extrude(context, id + "F1", {"entities" : qUnion([Q0]), "depth" : 860 * mm});
        }
        {
            var Q0;
            Q0=qCreatedBy(makeId("Right.planeOp"),FACE);
            var sketch = newSketch(context, id + "F2", { "sketchPlane" : qUnion([Q0])});
            skLineSegment(sketch, "E7", {"start": v(100.86, 0) * mm, "end": v(-1111.02, 0) * mm, "construction": true});
            skLineSegment(sketch, "E8", {"start": v(-860, 215) * mm, "end": v(-832, 215) * mm});
            skLineSegment(sketch, "E9", {"start": v(-832, 215) * mm, "end": v(-832, 240.4) * mm});
            skLineSegment(sketch, "E10", {"start": v(-832, 240.4) * mm, "end": v(-860, 246.4) * mm});
            skLineSegment(sketch, "E11", {"start": v(-860, 246.4) * mm, "end": v(-860, 215) * mm});
            skLineSegment(sketch, "E12", {"start": v(-430, 0) * mm, "end": v(-430, 346.03) * mm, "construction": true});
            skLineSegment(sketch, "E13.MirrorCS", {"start": v(0, 246.4) * mm, "end": v(0, 215) * mm});
            skLineSegment(sketch, "E14.MirrorCS", {"start": v(0, 215) * mm, "end": v(-28, 215) * mm});
            skLineSegment(sketch, "E15.MirrorCS", {"start": v(-28, 215) * mm, "end": v(-28, 240.4) * mm});
            skLineSegment(sketch, "E16.MirrorCS", {"start": v(-28, 240.4) * mm, "end": v(0, 246.4) * mm});
            skSolve(sketch);
        }
        {
            var Q0;
            Q0 = qSketchRegion(id + "F2", true);
            var Q1;
            Q1=sQuery(id+"F2.wireOp",EDGE,"E7");
            revolve(context, id + "F3", {"operationType" : NewBodyOperationType.REMOVE, "entities" : qUnion([Q0]), "axis" : qUnion([Q1]), "revolveType" : RevolveType.FULL, "oppositeDirection" : true});
        }
        {
            var Q0;
            Q0=qCreatedBy(makeId("Right.planeOp"),FACE);
            var sketch = newSketch(context, id + "F4", { "sketchPlane" : qUnion([Q0])});
            skLineSegment(sketch, "E17", {"start": v(0, 0) * mm, "end": v(-27.93, 0) * mm});
            skPoint(sketch, "E18.0", {"position": v(0, 246.4) * mm});
            skPoint(sketch, "E19.0", {"position": v(0, 250.4) * mm});
            skPoint(sketch, "E20.0", {"position": v(-28, 240.4) * mm});
            skLineSegment(sketch, "E21", {"start": v(0, 246.4) * mm, "end": v(-28, 240.4) * mm});
            skLineSegment(sketch, "E22", {"start": v(-27.93, 0) * mm, "end": v(-28, 240.4) * mm});
            skLineSegment(sketch, "E23", {"start": v(32.03, 250.4) * mm, "end": v(32.03, 0) * mm});
            skLineSegment(sketch, "E24", {"start": v(32.03, 0) * mm, "end": v(-27.93, 0) * mm});
            skLineSegment(sketch, "E25", {"start": v(102.79, 0) * mm, "end": v(-138.7, 0) * mm, "construction": true});
            skLineSegment(sketch, "E26", {"start": v(0, 246.4) * mm, "end": v(0, 250.4) * mm});
            skLineSegment(sketch, "E27", {"start": v(0, 250.4) * mm, "end": v(0, 270.4) * mm});
            skLineSegment(sketch, "E28", {"start": v(0, 270.4) * mm, "end": v(32.03, 270.4) * mm});
            skLineSegment(sketch, "E29", {"start": v(32.03, 270.4) * mm, "end": v(32.03, 250.4) * mm});
            skSolve(sketch);
        }
        {
            var Q0;
            Q0 = qSketchRegion(id + "F4", true);
            var Q1;
            Q1=sQuery(id+"F4.wireOp",EDGE,"E25");
            revolve(context, id + "F5", {"entities" : qUnion([Q0]), "axis" : qUnion([Q1]), "revolveType" : RevolveType.FULL});
        }
    });
